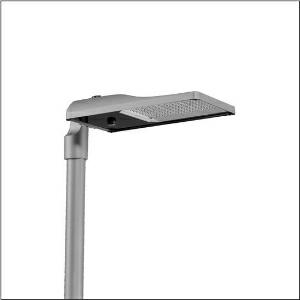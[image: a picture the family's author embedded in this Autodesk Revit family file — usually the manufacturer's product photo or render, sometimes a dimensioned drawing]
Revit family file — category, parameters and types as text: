
# Revit family: streetlight_sl_31_maxi___pl52_5xh8h31t08sa_1c4f
name_source: partatom
category: Lighting Fixtures
units: mm (PartAtom-declared; Revit-internal decimal feet)

## family parameters
Cut with Voids When Loaded = No
Host = Face
Light Source = No
Part Type = Normal
Room Calculation Point = No
Round Connector Dimension = Use Diameter
Shared = No

## types (1)
- --- (1 x LED, 27810 lm, 211.4 W, 3000K)
    Apparent Load = 211 VA
    CIE Flux Codes = 27 59 98 100 100
    Color Rendering = 70
    Color Temperature = 3000K
    Default Elevation = 1800 mm
    Description = Streetlight SL 31 maxi D4i, Desk-Remote mast luminaire for post-top, side-entry; light control with lens of PMMA; light distribution: PL52, direct asymmetric distribution, for standard-compliant lighting for roads and squares; LED: luminous flux: 27.810lm, light colour: 730, colour temperature: 3000K; luminous efficacy: 131,6lm/W; control: pre-setting: logarithmic dimming characteristic, flexible luminous flux parameterisation, time-dependent luminous flux control, constant luminous flux control, power reduction, intelligent temperature release in ECG and LED module, overheat protection; luminaire housing, of diecast aluminium, Siteco® metallic grey (DB 702S), corrosivity category C5 high according to DIN EN ISO 12944; cover of toughened safety glass, transparent, opened without tools; mast flange of diecast aluminium, Siteco® metallic grey (DB 702S), spigot size: 76/60mm, mast flange included unmounted; with cable H07RN-F 2x 1.5mm², cable length: 14,5m, connection cable pre-assembled; mains connection: 220..240V, AC, 50/60Hz; power consumption (at start of service life): 211,4W / (at end of service life): 238W / (with reduced operation 50%): 88,1W; protection rating (complete): IP66; insulation class (complete): insulation class II (safety insulation); impact resistance: IK09; certification: CE, ENEC, ENEC+, VDE, UKCA, ZD4i; permissible operating ambient temperature for outdoor applications: -40..+50°C; packaging unit: 1 piece

Light Distribution: PL52
    Height = 79 mm
    Lamp = 1 x LED
    Lamp Light Flux = 27810 lm
    Lamp Power = 211.4 W
    Lamp count = 1
    Length = 657 mm
    Luminous efficacy = 132 lm/W
    Manufacturer = Siteco
    ModVariant = No
    Model = 5XH8H31T08SA
    Number of Poles = 1
    OnlyDefault = Yes
    Power Factor = 1
    Product Name = Streetlight SL 31 maxi | PL52
    Product group = mast luminaire | pylon top
    ProductGroupID = 6100
    Protection Class = Protection class II
    Protection Degree = IP 66
    RLX_Detail_Level = 1
    RLX_Emergency_Light_Flux = 0 lm
    RLX_Emergency_Type = 0
    RLX_Emergency_Type_DB = No
    RlxData = <blob elided: 56789 chars, md5=62fa8b90>
    Socket = socket
    Standby Power = 0 W
    System Light Flux = 27810 lm
    System Power = 211 W
    Type Comments = factory setting: luminous flux: 100 % | dim-lin: 254 | 727 mA
    Type Image = l_1300303.jpg
    URL = http://relux.com
    VarID = @adj_039972
    Voltage = 0 V
    Weight = 0.00 kg
    Width = 362 mm

## geometry (parser evidence)
native form markers: Blend x4, Sweep x11
no freeform markers — native parametric forms only
